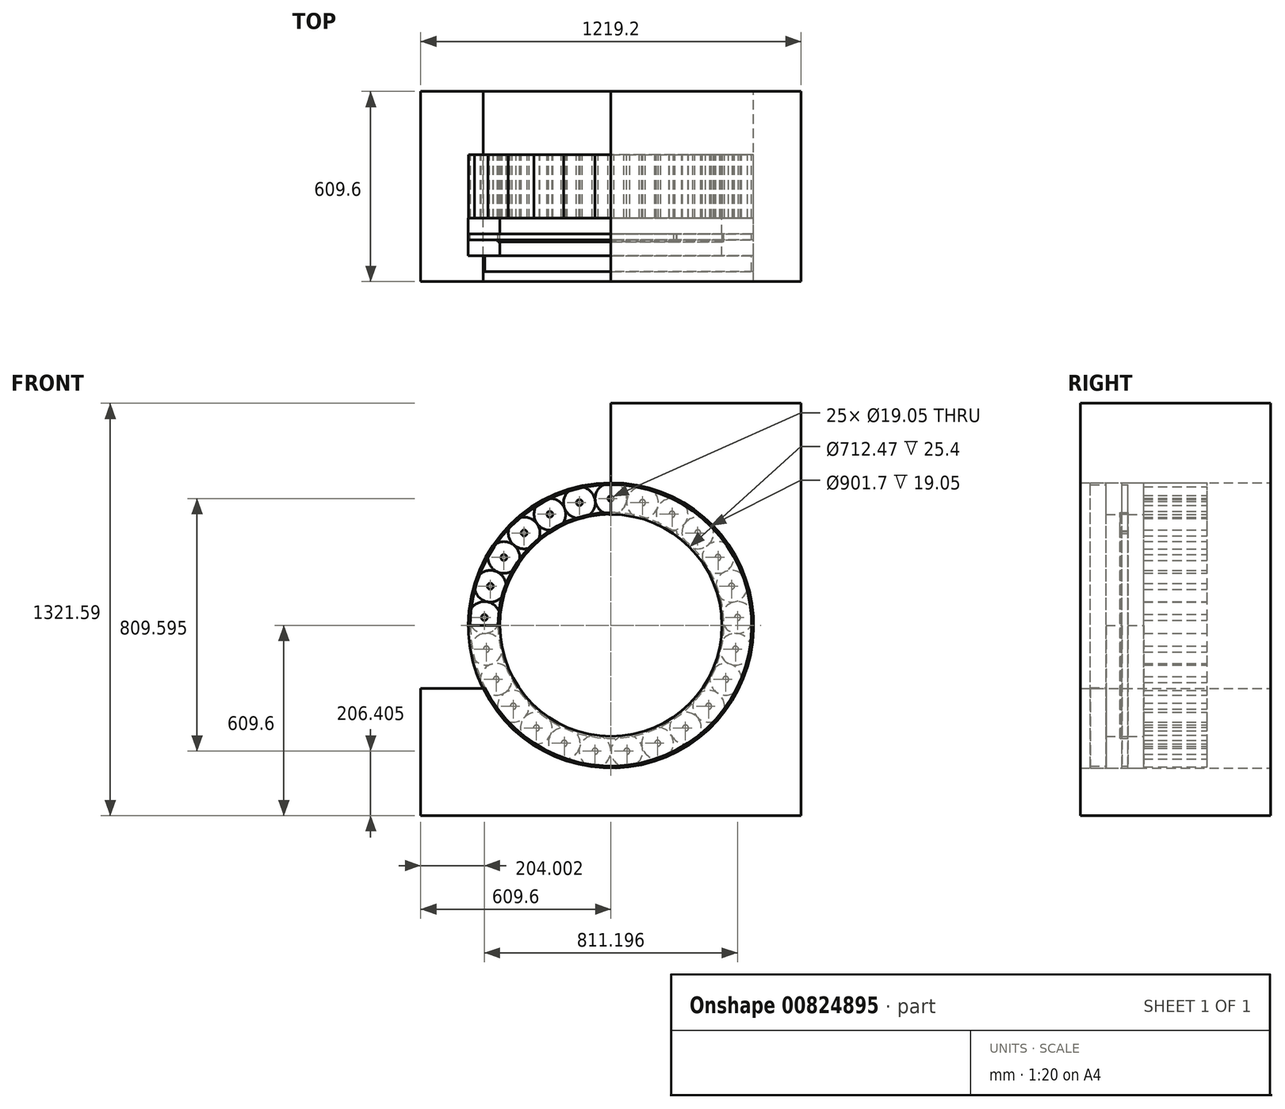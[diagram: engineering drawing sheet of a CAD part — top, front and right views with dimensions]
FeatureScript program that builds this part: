
annotation { "Feature Type Name" : "Feature", "Feature Type Description" : "" }
export const myFeature = defineFeature(function(context is Context, id is Id, definition is map)
    precondition{}
    {
        {
            var Q0;
            Q0=qCreatedBy(makeId("Front.planeOp"),FACE);
            var sketch = newSketch(context, id + "F0", { "sketchPlane" : qUnion([Q0])});
            skLineSegment(sketch, "E0", {"start": v(0, -609.6) * mm, "end": v(609.6, -609.6) * mm});
            skLineSegment(sketch, "E1.bottom", {"start": v(0, 712) * mm, "end": v(609.6, 712) * mm});
            skLineSegment(sketch, "E1.top", {"start": v(-609.6, -609.6) * mm, "end": v(609.6, -609.6) * mm});
            skLineSegment(sketch, "E1.left", {"start": v(-609.6, -202.4) * mm, "end": v(-609.6, -609.6) * mm});
            skLineSegment(sketch, "E1.right", {"start": v(609.6, 712) * mm, "end": v(609.6, -609.6) * mm});
            skArc(sketch, "E2", {"start": v(-409.95, -202.4) * mm, "mid": v(388.31, -241.34) * mm, "end": v(0, 457.2) * mm});
            skLineSegment(sketch, "E3", {"start": v(-609.6, -202.4) * mm, "end": v(-409.95, -202.4) * mm});
            skLineSegment(sketch, "E4", {"start": v(0, 457.2) * mm, "end": v(0, 712) * mm});
            skSolve(sketch);
        }
        {
            var Q0;
            Q0=makeQuery(id+"F0.imprint","IMPRINT",FACE,{"disambiguationData":[TD([[makeQuery(id+"F0.imprint","IMPRINT",EDGE,{"derivedFrom":sQuery(id+"F0.wireOp",EDGE,"E1.bottom")}),-1.0]])]});
            extrude(context, id + "F1", {"entities" : qUnion([Q0]), "endBound" : BoundingType.SYMMETRIC, "depth" : 609.6 * mm, "offsetDistance" : 25.4 * mm});
        }
        {
            var Q0;
            Q0=qCreatedBy(makeId("Front.planeOp"),FACE);
            var sketch = newSketch(context, id + "F2", { "sketchPlane" : qUnion([Q0])});
            skCircle(sketch, "E5", {"center": v(0, 0) * mm, "radius": 355.6 * mm});
            skCircle(sketch, "E6", {"center": v(0, 0) * mm, "radius": 342.9 * mm});
            skSolve(sketch);
        }
        {
            var Q0;
            Q0=sQuery(id+"F2.wireOp",EDGE,"E6");
            var Q1;
            Q1=sQuery(id+"F2.wireOp",EDGE,"E5");
            extrude(context, id + "F3", {"bodyType" : ToolBodyType.SURFACE, "surfaceEntities" : qUnion([Q0, Q1]), "endBound" : BoundingType.SYMMETRIC, "depth" : 1219.2 * mm, "offsetDistance" : 25.4 * mm});
        }
        {
            var Q0;
            Q0=qCreatedBy(makeId("Front.planeOp"),FACE);
            var sketch = newSketch(context, id + "F4", { "sketchPlane" : qUnion([Q0])});
            skCircle(sketch, "E7", {"center": v(0, 406.4) * mm, "radius": 50.8 * mm});
            skCircle(sketch, "E8", {"center": v(0, 406.4) * mm, "radius": 9.53 * mm});
            skCircle(sketch, "E9.1.0", {"center": v(-101.07, 393.63) * mm, "radius": 50.8 * mm});
            skCircle(sketch, "E9.1.1", {"center": v(-101.07, 393.63) * mm, "radius": 9.52 * mm});
            skCircle(sketch, "E9.2.0", {"center": v(-195.78, 356.13) * mm, "radius": 50.8 * mm});
            skCircle(sketch, "E9.2.1", {"center": v(-195.78, 356.13) * mm, "radius": 9.53 * mm});
            skPoint(sketch, "E9.center", {"position": v(0, 0) * mm});
            skCircle(sketch, "E10.1.3.0", {"center": v(-278.2, 296.25) * mm, "radius": 50.8 * mm});
            skCircle(sketch, "E10.2.3.0", {"center": v(-278.2, 296.25) * mm, "radius": 9.53 * mm});
            skCircle(sketch, "E10.1.4.0", {"center": v(-343.13, 217.76) * mm, "radius": 50.8 * mm});
            skCircle(sketch, "E10.2.4.0", {"center": v(-343.13, 217.76) * mm, "radius": 9.53 * mm});
            skCircle(sketch, "E10.1.5.0", {"center": v(-386.5, 125.58) * mm, "radius": 50.8 * mm});
            skCircle(sketch, "E10.2.5.0", {"center": v(-386.5, 125.58) * mm, "radius": 9.53 * mm});
            skCircle(sketch, "E10.1.6.0", {"center": v(-405.6, 25.52) * mm, "radius": 50.8 * mm});
            skCircle(sketch, "E10.2.6.0", {"center": v(-405.6, 25.52) * mm, "radius": 9.53 * mm});
            skCircle(sketch, "E10.1.7.0", {"center": v(-399.2, -76.15) * mm, "radius": 50.8 * mm});
            skCircle(sketch, "E10.2.7.0", {"center": v(-399.2, -76.15) * mm, "radius": 9.53 * mm});
            skCircle(sketch, "E10.1.8.0", {"center": v(-367.72, -173.04) * mm, "radius": 50.8 * mm});
            skCircle(sketch, "E10.2.8.0", {"center": v(-367.72, -173.04) * mm, "radius": 9.53 * mm});
            skCircle(sketch, "E10.1.9.0", {"center": v(-313.14, -259.05) * mm, "radius": 50.8 * mm});
            skCircle(sketch, "E10.2.9.0", {"center": v(-313.14, -259.05) * mm, "radius": 9.53 * mm});
            skCircle(sketch, "E10.1.10.0", {"center": v(-238.88, -328.78) * mm, "radius": 50.8 * mm});
            skCircle(sketch, "E10.2.10.0", {"center": v(-238.88, -328.78) * mm, "radius": 9.53 * mm});
            skCircle(sketch, "E10.1.11.0", {"center": v(-149.6, -377.86) * mm, "radius": 50.8 * mm});
            skCircle(sketch, "E10.2.11.0", {"center": v(-149.6, -377.86) * mm, "radius": 9.53 * mm});
            skCircle(sketch, "E10.1.12.0", {"center": v(-50.94, -403.2) * mm, "radius": 50.8 * mm});
            skCircle(sketch, "E10.2.12.0", {"center": v(-50.94, -403.2) * mm, "radius": 9.53 * mm});
            skCircle(sketch, "E10.1.13.0", {"center": v(50.94, -403.2) * mm, "radius": 50.8 * mm});
            skCircle(sketch, "E10.2.13.0", {"center": v(50.94, -403.2) * mm, "radius": 9.53 * mm});
            skCircle(sketch, "E10.1.14.0", {"center": v(149.6, -377.86) * mm, "radius": 50.8 * mm});
            skCircle(sketch, "E10.2.14.0", {"center": v(149.6, -377.86) * mm, "radius": 9.53 * mm});
            skCircle(sketch, "E10.1.15.0", {"center": v(238.88, -328.78) * mm, "radius": 50.8 * mm});
            skCircle(sketch, "E10.2.15.0", {"center": v(238.88, -328.78) * mm, "radius": 9.53 * mm});
            skCircle(sketch, "E10.1.16.0", {"center": v(313.14, -259.05) * mm, "radius": 50.8 * mm});
            skCircle(sketch, "E10.2.16.0", {"center": v(313.14, -259.05) * mm, "radius": 9.53 * mm});
            skCircle(sketch, "E10.1.17.0", {"center": v(367.72, -173.04) * mm, "radius": 50.8 * mm});
            skCircle(sketch, "E10.2.17.0", {"center": v(367.72, -173.04) * mm, "radius": 9.53 * mm});
            skCircle(sketch, "E10.1.18.0", {"center": v(399.2, -76.15) * mm, "radius": 50.8 * mm});
            skCircle(sketch, "E10.2.18.0", {"center": v(399.2, -76.15) * mm, "radius": 9.53 * mm});
            skCircle(sketch, "E10.1.19.0", {"center": v(405.6, 25.52) * mm, "radius": 50.8 * mm});
            skCircle(sketch, "E10.2.19.0", {"center": v(405.6, 25.52) * mm, "radius": 9.53 * mm});
            skCircle(sketch, "E10.1.20.0", {"center": v(386.5, 125.58) * mm, "radius": 50.8 * mm});
            skCircle(sketch, "E10.2.20.0", {"center": v(386.5, 125.58) * mm, "radius": 9.53 * mm});
            skCircle(sketch, "E10.1.21.0", {"center": v(343.13, 217.76) * mm, "radius": 50.8 * mm});
            skCircle(sketch, "E10.2.21.0", {"center": v(343.13, 217.76) * mm, "radius": 9.53 * mm});
            skCircle(sketch, "E10.1.22.0", {"center": v(278.2, 296.25) * mm, "radius": 50.8 * mm});
            skCircle(sketch, "E10.2.22.0", {"center": v(278.2, 296.25) * mm, "radius": 9.53 * mm});
            skCircle(sketch, "E10.1.23.0", {"center": v(195.78, 356.13) * mm, "radius": 50.8 * mm});
            skCircle(sketch, "E10.2.23.0", {"center": v(195.78, 356.13) * mm, "radius": 9.53 * mm});
            skCircle(sketch, "E10.1.24.0", {"center": v(101.07, 393.63) * mm, "radius": 50.8 * mm});
            skCircle(sketch, "E10.2.24.0", {"center": v(101.07, 393.63) * mm, "radius": 9.53 * mm});
            skSolve(sketch);
        }
        {
            var Q0;
            Q0 = qSketchRegion(id + "F4", true);
            extrude(context, id + "F5", {"entities" : qUnion([Q0]), "operationType" : NewBodyOperationType.ADD, "endBound" : BoundingType.SYMMETRIC, "depth" : 203.2 * mm, "offsetDistance" : 25.4 * mm});
        }
        {
            var Q0;
            Q0=makeQuery(id+"F5.opExtrude","CAP_FACE",FACE,{"disambiguationData":[OSD([sQuery(id+"F4.wireOp",EDGE,"E7"),sQuery(id+"F4.wireOp",EDGE,"E8")])],"isStart":false});
            var sketch = newSketch(context, id + "F6", { "sketchPlane" : qUnion([Q0])});
            skArc(sketch, "E11", {"start": v(-355.6, 0) * mm, "mid": v(251.45, -251.45) * mm, "end": v(0, 355.6) * mm});
            skArc(sketch, "E12", {"start": v(-457.2, 0) * mm, "mid": v(323.29, -323.29) * mm, "end": v(0, 457.2) * mm});
            skLineSegment(sketch, "E13", {"start": v(-355.6, 0) * mm, "end": v(-457.2, 0) * mm});
            skLineSegment(sketch, "E14", {"start": v(0, 355.6) * mm, "end": v(0, 457.2) * mm});
            skSolve(sketch);
        }
        {
            var Q0;
            Q0 = qSketchRegion(id + "F6", true);
            extrude(context, id + "F7", {"entities" : qUnion([Q0]), "depth" : 50.8 * mm, "offsetDistance" : 25.4 * mm});
        }
        {
            var Q0;
            Q0=makeQuery(id+"F7.opExtrude","CAP_FACE",FACE,{"disambiguationData":[OSD([sQuery(id+"F6.wireOp",EDGE,"E11"),sQuery(id+"F6.wireOp",EDGE,"E12")])],"isStart":false});
            var sketch = newSketch(context, id + "F8", { "sketchPlane" : qUnion([Q0])});
            skCircle(sketch, "E15", {"center": v(0, 0) * mm, "radius": 361.95 * mm});
            skCircle(sketch, "E16", {"center": v(0, 0) * mm, "radius": 356.24 * mm});
            skCircle(sketch, "E17", {"center": v(206.24, 297.44) * mm, "radius": 5.72 * mm});
            skSolve(sketch);
        }
        {
            var Q0;
            Q0=makeQuery(id+"F7.opExtrude","CAP_FACE",FACE,{"disambiguationData":[OSD([sQuery(id+"F6.wireOp",EDGE,"E11"),sQuery(id+"F6.wireOp",EDGE,"E12")])],"isStart":false});
            var sketch = newSketch(context, id + "F9", { "sketchPlane" : qUnion([Q0])});
            skCircle(sketch, "E18", {"center": v(0, 0) * mm, "radius": 457.2 * mm});
            skCircle(sketch, "E19", {"center": v(0, 0) * mm, "radius": 450.85 * mm});
            skSolve(sketch);
        }
        {
            var Q0;
            Q0=makeQuery(id+"F9.imprint","IMPRINT",FACE,{"disambiguationData":[TD([[makeQuery(id+"F9.imprint","IMPRINT",EDGE,{"derivedFrom":sQuery(id+"F9.wireOp",EDGE,"E18")}),1.0]])]});
            var Q1;
            Q1=sQuery(id+"F9.wireOp",EDGE,"E19");
            var Q2;
            Q2=sQuery(id+"F9.wireOp",EDGE,"E18");
            extrude(context, id + "F10", {"entities" : qUnion([Q0]), "surfaceEntities" : qUnion([Q1, Q2]), "depth" : 19.05 * mm, "offsetDistance" : 25.4 * mm});
        }
        {
            var Q0;
            Q0 = qSketchRegion(id + "F8", true);
            extrude(context, id + "F11", {"entities" : qUnion([Q0]), "operationType" : NewBodyOperationType.ADD, "depth" : 25.4 * mm, "offsetDistance" : 25.4 * mm});
        }
        {
            var Q0;
            Q0=makeQuery(id+"F10.opExtrude","CAP_FACE",FACE,{"disambiguationData":[OSD([sQuery(id+"F9.wireOp",EDGE,"E18"),sQuery(id+"F9.wireOp",EDGE,"E19")])],"isStart":false});
            var sketch = newSketch(context, id + "F12", { "sketchPlane" : qUnion([Q0])});
            skArc(sketch, "E20", {"start": v(-457.2, 0) * mm, "mid": v(323.29, -323.29) * mm, "end": v(0, 457.2) * mm});
            skArc(sketch, "E21", {"start": v(-355.6, 0) * mm, "mid": v(251.45, -251.45) * mm, "end": v(0, 355.6) * mm});
            skLineSegment(sketch, "E22", {"start": v(0, 355.6) * mm, "end": v(0, 457.2) * mm});
            skLineSegment(sketch, "E23", {"start": v(-355.6, 0) * mm, "end": v(-457.2, 0) * mm});
            skSolve(sketch);
        }
        {
            var Q0;
            Q0 = qSketchRegion(id + "F12", true);
            extrude(context, id + "F13", {"entities" : qUnion([Q0]), "depth" : 50.8 * mm, "offsetDistance" : 25.4 * mm});
        }
        {
            var Q0;
            Q0=makeQuery(id+"F13.opExtrude","CAP_FACE",FACE,{"disambiguationData":[OSD([sQuery(id+"F12.wireOp",EDGE,"E20"),sQuery(id+"F12.wireOp",EDGE,"E21"),sQuery(id+"F12.wireOp",EDGE,"E22"),sQuery(id+"F12.wireOp",EDGE,"E23")])],"isStart":false});
            var sketch = newSketch(context, id + "F14", { "sketchPlane" : qUnion([Q0])});
            skArc(sketch, "E24", {"start": v(-404.23, -199.66) * mm, "mid": v(382.94, -237.96) * mm, "end": v(0, 450.85) * mm});
            skLineSegment(sketch, "E25", {"start": v(-404.23, -199.66) * mm, "end": v(-409.92, -202.47) * mm});
            skLineSegment(sketch, "E26", {"start": v(0, 450.85) * mm, "end": v(0, 457.2) * mm});
            skArc(sketch, "E27", {"start": v(-409.92, -202.47) * mm, "mid": v(388.33, -241.31) * mm, "end": v(0, 457.2) * mm});
            skSolve(sketch);
        }
        {
            var Q0;
            Q0=makeQuery(id+"F14.imprint","IMPRINT",FACE,{"disambiguationData":[TD([[makeQuery(id+"F14.imprint","IMPRINT",EDGE,{"derivedFrom":sQuery(id+"F14.wireOp",EDGE,"E24")}),-1.0]])]});
            extrude(context, id + "F15", {"entities" : qUnion([Q0]), "depth" : 50.8 * mm, "offsetDistance" : 25.4 * mm});
        }
    });
